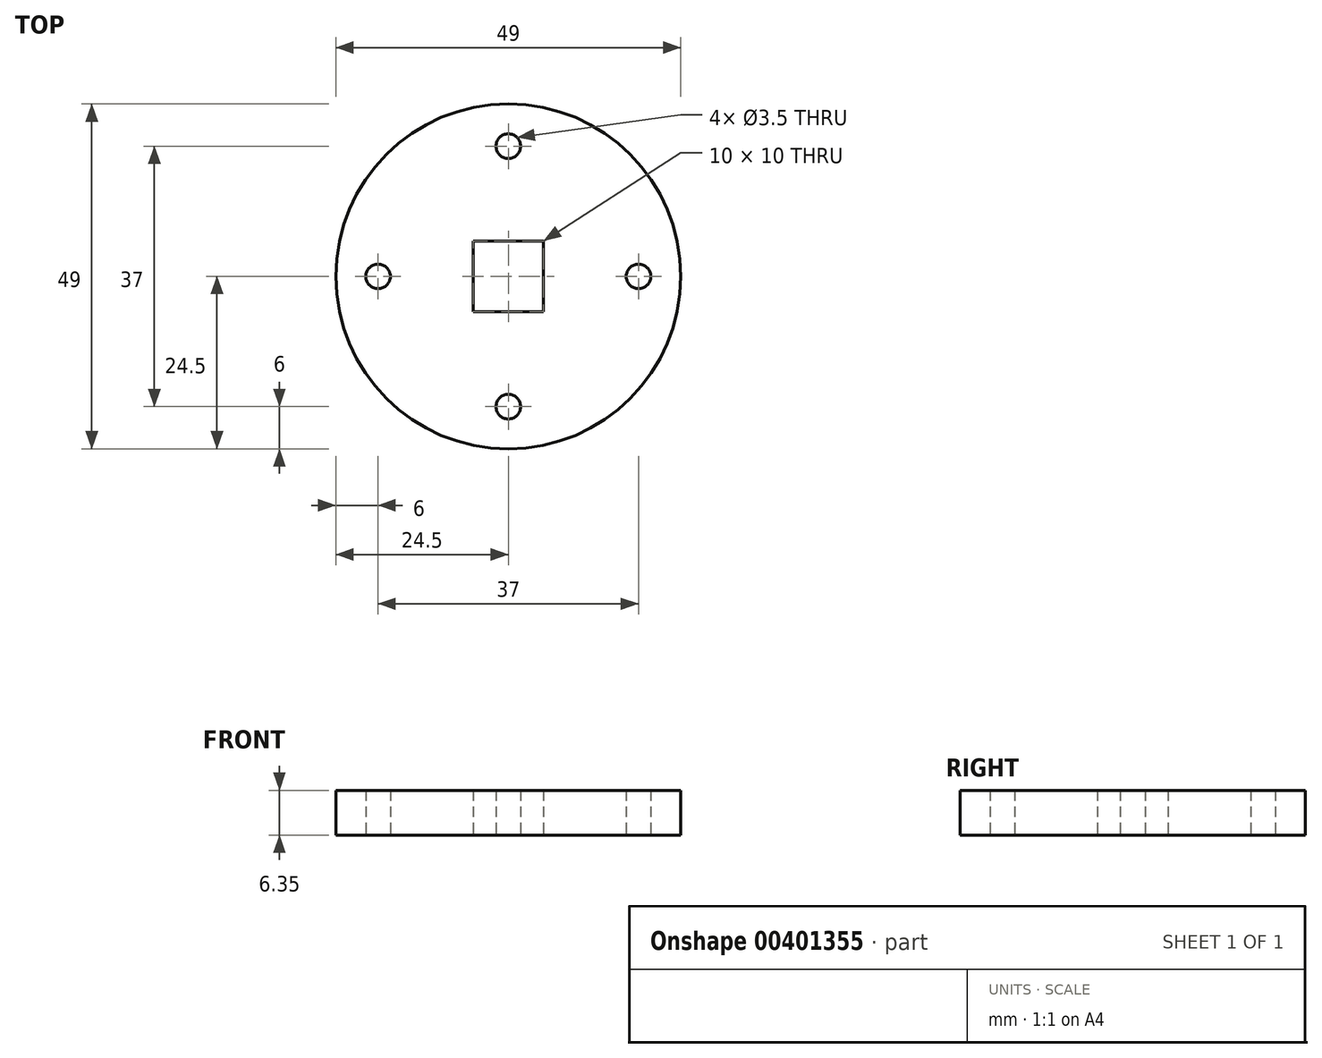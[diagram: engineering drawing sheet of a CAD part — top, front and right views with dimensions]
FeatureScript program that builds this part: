
annotation { "Feature Type Name" : "Feature", "Feature Type Description" : "" }
export const myFeature = defineFeature(function(context is Context, id is Id, definition is map)
    precondition{}
    {
        {
            var Q0;
            Q0=qCreatedBy(makeId("Top.planeOp"),FACE);
            var sketch = newSketch(context, id + "F0", { "sketchPlane" : qUnion([Q0])});
            skCircle(sketch, "E0", {"center": v(0, 0) * mm, "radius": 24.5 * mm});
            skLineSegment(sketch, "E1", {"start": v(0, 24.5) * mm, "end": v(0, -24.5) * mm, "construction": true});
            skLineSegment(sketch, "E2", {"start": v(-24.5, 0) * mm, "end": v(24.5, 0) * mm, "construction": true});
            skCircle(sketch, "E3", {"center": v(-18.5, 0) * mm, "radius": 1.75 * mm});
            skCircle(sketch, "E4", {"center": v(0, 18.5) * mm, "radius": 1.75 * mm});
            skCircle(sketch, "E5", {"center": v(18.5, 0) * mm, "radius": 1.75 * mm});
            skCircle(sketch, "E6", {"center": v(0, -18.5) * mm, "radius": 1.75 * mm});
            skLineSegment(sketch, "E7.bottom", {"start": v(-5, 5) * mm, "end": v(5, 5) * mm});
            skLineSegment(sketch, "E7.top", {"start": v(-5, -5) * mm, "end": v(5, -5) * mm});
            skLineSegment(sketch, "E7.left", {"start": v(-5, 5) * mm, "end": v(-5, -5) * mm});
            skLineSegment(sketch, "E7.right", {"start": v(5, 5) * mm, "end": v(5, -5) * mm});
            skSolve(sketch);
        }
        {
            var Q0;
            Q0=makeQuery(id+"F0.imprint","IMPRINT",FACE,{"disambiguationData":[TD([[makeQuery(id+"F0.imprint","IMPRINT",EDGE,{"derivedFrom":sQuery(id+"F0.wireOp",EDGE,"E0")}),1.0]])]});
            extrude(context, id + "F1", {"entities" : qUnion([Q0]), "depth" : 6.35 * mm, "offsetDistance" : 25 * mm});
        }
    });
